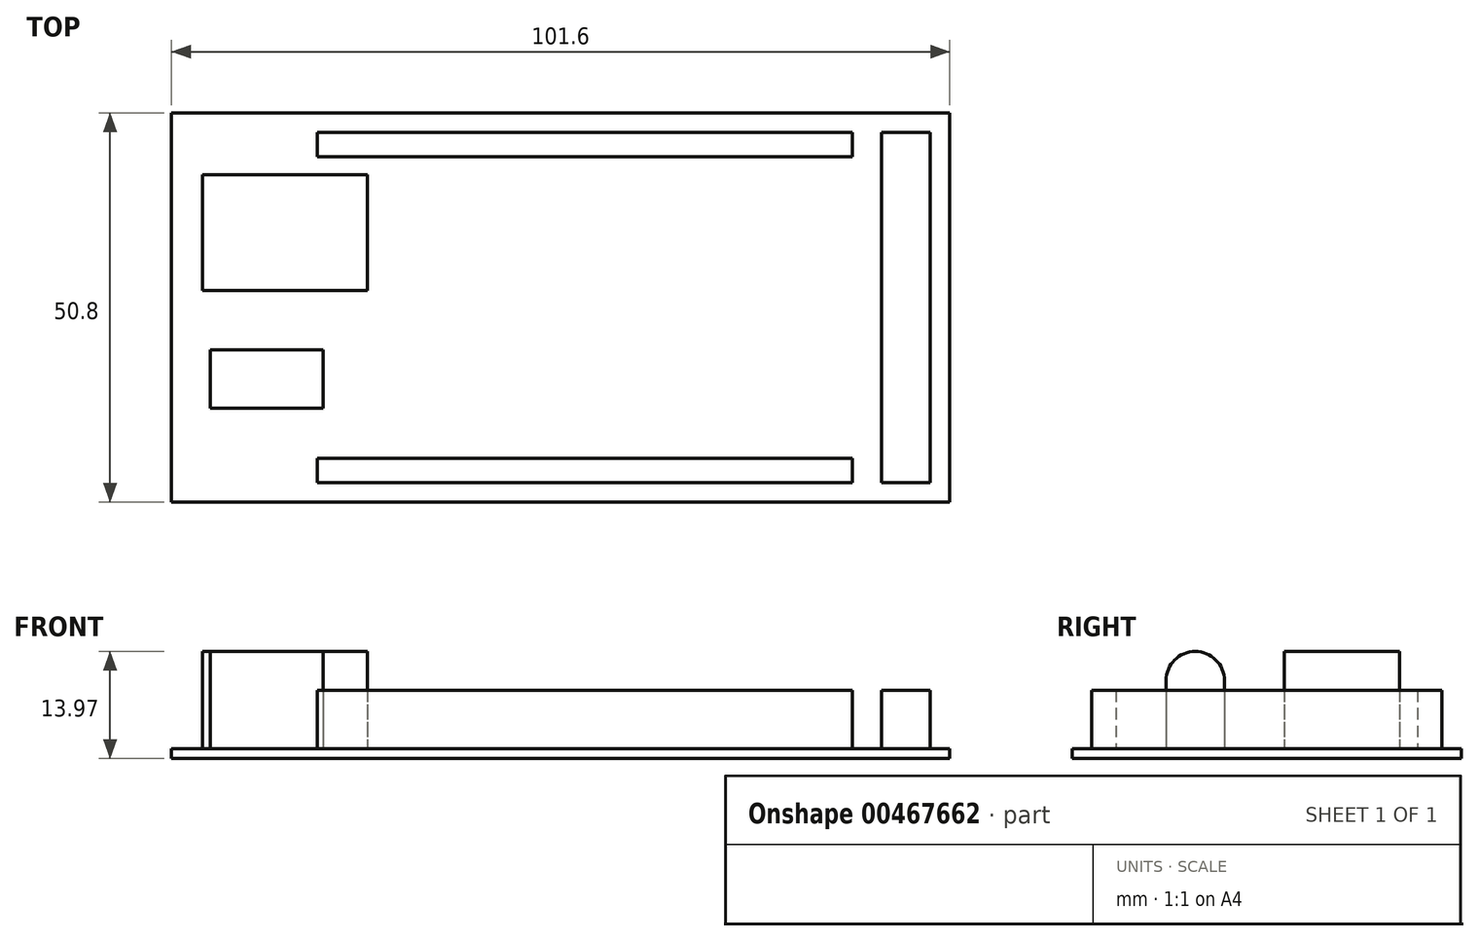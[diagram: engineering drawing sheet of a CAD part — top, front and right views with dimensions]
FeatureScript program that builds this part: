
annotation { "Feature Type Name" : "Feature", "Feature Type Description" : "" }
export const myFeature = defineFeature(function(context is Context, id is Id, definition is map)
    precondition{}
    {
        {
            var Q0;
            Q0=qCreatedBy(makeId("Top.planeOp"),FACE);
            var sketch = newSketch(context, id + "F0", { "sketchPlane" : qUnion([Q0])});
            skLineSegment(sketch, "E0.bottom", {"start": v(50.8, 25.4) * mm, "end": v(-50.8, 25.4) * mm});
            skLineSegment(sketch, "E0.top", {"start": v(50.8, -25.4) * mm, "end": v(-50.8, -25.4) * mm});
            skLineSegment(sketch, "E0.left", {"start": v(50.8, 25.4) * mm, "end": v(50.8, -25.4) * mm});
            skLineSegment(sketch, "E0.right", {"start": v(-50.8, 25.4) * mm, "end": v(-50.8, -25.4) * mm});
            skPoint(sketch, "E0.middle", {"position": v(0, 0) * mm});
            skSolve(sketch);
        }
        {
            var Q0;
            Q0=makeQuery(id+"F0.imprint","IMPRINT",FACE,{"disambiguationData":[TD([[makeQuery(id+"F0.imprint","IMPRINT",EDGE,{"derivedFrom":sQuery(id+"F0.wireOp",EDGE,"E0.bottom")}),1.0]])]});
            extrude(context, id + "F1", {"entities" : qUnion([Q0]), "depth" : 1.27 * mm});
        }
        {
            var Q0;
            Q0=makeQuery(id+"F1.opExtrude","CAP_FACE",FACE,{"disambiguationData":[OSD([sQuery(id+"F0.wireOp",EDGE,"E0.bottom"),sQuery(id+"F0.wireOp",EDGE,"E0.top"),sQuery(id+"F0.wireOp",EDGE,"E0.left"),sQuery(id+"F0.wireOp",EDGE,"E0.right")])],"isStart":false});
            var sketch = newSketch(context, id + "F2", { "sketchPlane" : qUnion([Q0])});
            skLineSegment(sketch, "E1.bottom", {"start": v(-31.75, 22.86) * mm, "end": v(38.1, 22.86) * mm});
            skLineSegment(sketch, "E1.top", {"start": v(-31.75, 19.68) * mm, "end": v(38.1, 19.68) * mm});
            skLineSegment(sketch, "E1.left", {"start": v(-31.75, 22.86) * mm, "end": v(-31.75, 19.68) * mm});
            skLineSegment(sketch, "E1.right", {"start": v(38.1, 22.86) * mm, "end": v(38.1, 19.69) * mm});
            skLineSegment(sketch, "E2.bottom", {"start": v(41.91, 22.86) * mm, "end": v(48.26, 22.86) * mm});
            skLineSegment(sketch, "E2.top", {"start": v(41.91, -22.86) * mm, "end": v(48.26, -22.86) * mm});
            skLineSegment(sketch, "E2.left", {"start": v(41.91, 22.86) * mm, "end": v(41.91, -22.86) * mm});
            skLineSegment(sketch, "E2.right", {"start": v(48.26, 22.86) * mm, "end": v(48.26, -22.86) * mm});
            skLineSegment(sketch, "E3.bottom", {"start": v(38.1, -19.69) * mm, "end": v(-31.75, -19.69) * mm});
            skLineSegment(sketch, "E3.top", {"start": v(38.1, -22.86) * mm, "end": v(-31.75, -22.86) * mm});
            skLineSegment(sketch, "E3.left", {"start": v(38.1, -19.69) * mm, "end": v(38.1, -22.86) * mm});
            skLineSegment(sketch, "E3.right", {"start": v(-31.75, -19.69) * mm, "end": v(-31.75, -22.86) * mm});
            skSolve(sketch);
        }
        {
            var Q0;
            Q0 = qSketchRegion(id + "F2", true);
            extrude(context, id + "F3", {"entities" : qUnion([Q0]), "operationType" : NewBodyOperationType.ADD, "depth" : 7.62 * mm});
        }
        {
            var Q0;
            Q0=makeQuery(id+"F1.opExtrude","CAP_FACE",FACE,{"disambiguationData":[OSD([sQuery(id+"F0.wireOp",EDGE,"E0.bottom"),sQuery(id+"F0.wireOp",EDGE,"E0.top"),sQuery(id+"F0.wireOp",EDGE,"E0.left"),sQuery(id+"F0.wireOp",EDGE,"E0.right")])],"isStart":false});
            var sketch = newSketch(context, id + "F4", { "sketchPlane" : qUnion([Q0])});
            skLineSegment(sketch, "E4.bottom", {"start": v(-46.75, 17.3) * mm, "end": v(-25.22, 17.3) * mm});
            skLineSegment(sketch, "E4.top", {"start": v(-46.75, 2.25) * mm, "end": v(-25.22, 2.25) * mm});
            skLineSegment(sketch, "E4.left", {"start": v(-46.75, 17.3) * mm, "end": v(-46.75, 2.25) * mm});
            skLineSegment(sketch, "E4.right", {"start": v(-25.22, 17.3) * mm, "end": v(-25.22, 2.25) * mm});
            skLineSegment(sketch, "E5.bottom", {"start": v(-45.73, -5.55) * mm, "end": v(-30.97, -5.55) * mm});
            skLineSegment(sketch, "E5.top", {"start": v(-45.73, -13.17) * mm, "end": v(-30.97, -13.17) * mm});
            skLineSegment(sketch, "E5.left", {"start": v(-45.73, -5.55) * mm, "end": v(-45.73, -13.17) * mm});
            skLineSegment(sketch, "E5.right", {"start": v(-30.97, -5.55) * mm, "end": v(-30.97, -13.17) * mm});
            skSolve(sketch);
        }
        {
            var Q0;
            Q0 = qSketchRegion(id + "F4", true);
            extrude(context, id + "F5", {"entities" : qUnion([Q0]), "operationType" : NewBodyOperationType.ADD, "depth" : 12.7 * mm});
        }
        {
            var Q0;
            Q0=makeQuery(id+"F5.opExtrude","CAP_EDGE",EDGE,{"disambiguationData":[OSD([sQuery(id+"F4.wireOp",EDGE,"E5.top")])],"isStart":false});
            var Q1;
            Q1=makeQuery(id+"F5.opExtrude","CAP_EDGE",EDGE,{"disambiguationData":[OSD([sQuery(id+"F4.wireOp",EDGE,"E5.bottom")])],"isStart":false});
            fillet(context, id + "F6", {"entities" : qUnion([Q0, Q1]), "radius" : 3.8 * mm, "tangentPropagation" : true, "allowEdgeOverflow" : false});
        }
    });
